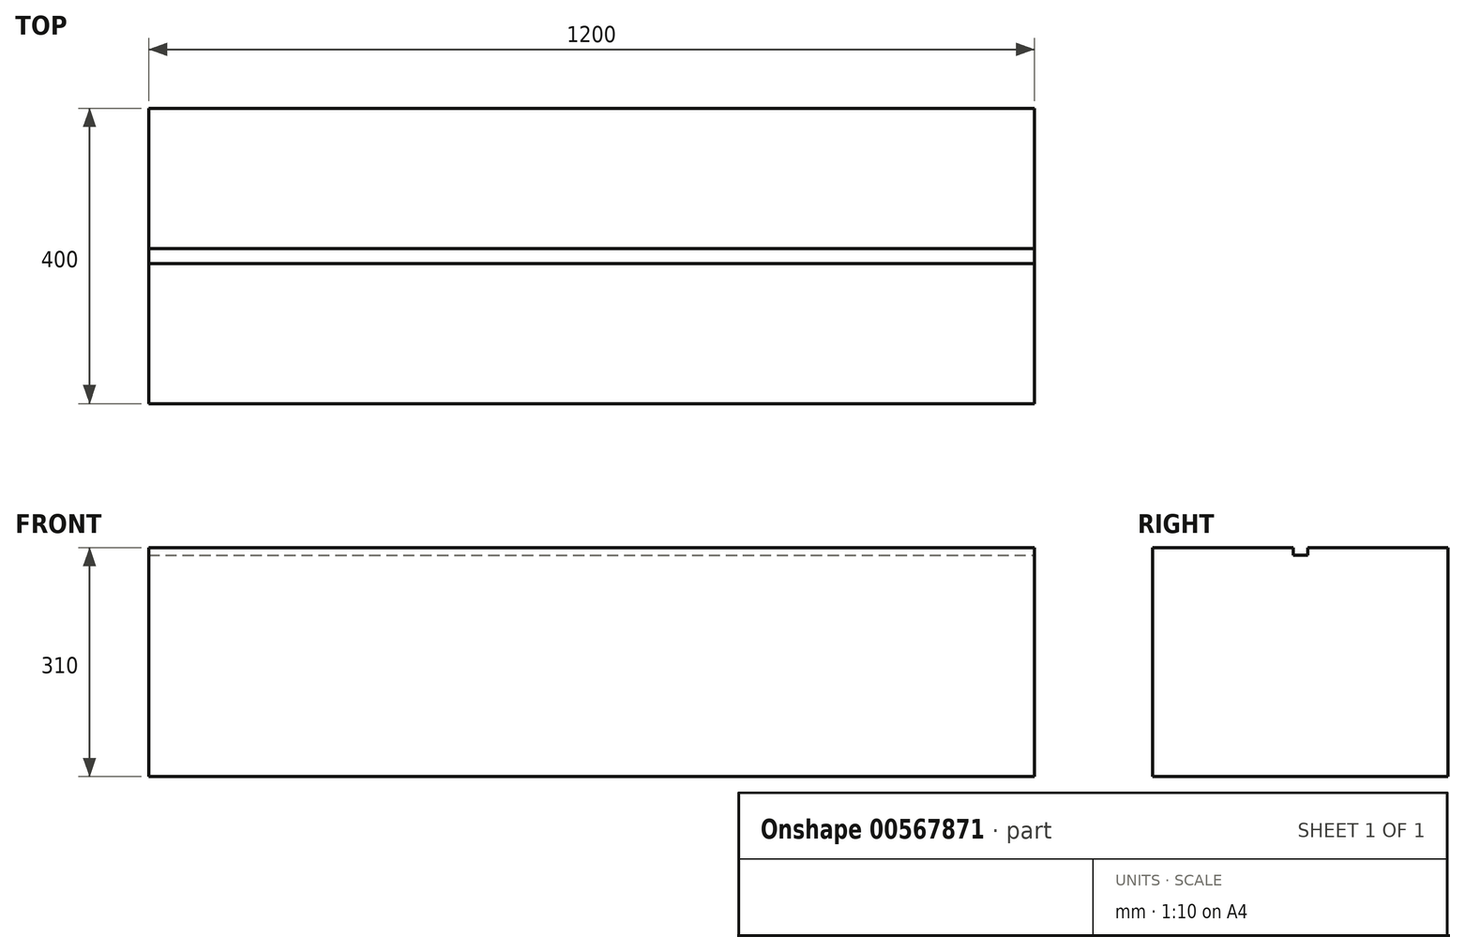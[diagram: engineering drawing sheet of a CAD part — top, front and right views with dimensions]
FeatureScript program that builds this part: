
annotation { "Feature Type Name" : "Feature", "Feature Type Description" : "" }
export const myFeature = defineFeature(function(context is Context, id is Id, definition is map)
    precondition{}
    {
        {
            var Q0;
            Q0=qCreatedBy(makeId("Right.planeOp"),FACE);
            var sketch = newSketch(context, id + "F0", { "sketchPlane" : qUnion([Q0])});
            skLineSegment(sketch, "E0.bottom", {"start": v(-160.6, 173.56) * mm, "end": v(239.4, 173.56) * mm});
            skLineSegment(sketch, "E0.top", {"start": v(-160.6, -136.44) * mm, "end": v(239.4, -136.44) * mm});
            skLineSegment(sketch, "E0.left", {"start": v(-160.6, 173.56) * mm, "end": v(-160.6, -136.44) * mm});
            skLineSegment(sketch, "E0.right", {"start": v(239.4, 173.56) * mm, "end": v(239.4, -136.44) * mm});
            skSolve(sketch);
        }
        {
            var Q0;
            Q0=qSketchRegion(id+"F0",true);
            extrude(context, id + "F1", {"entities" : qUnion([Q0]), "oppositeDirection" : true, "depth" : 1200 * mm, "offsetDistance" : 25 * mm});
        }
        {
            var Q0;
            Q0=makeQuery(id+"F1.opExtrude","CAP_FACE",FACE,{"disambiguationData":[OSD([sQuery(id+"F0.wireOp",EDGE,"E0.bottom"),sQuery(id+"F0.wireOp",EDGE,"E0.top"),sQuery(id+"F0.wireOp",EDGE,"E0.left"),sQuery(id+"F0.wireOp",EDGE,"E0.right")])],"isStart":true});
            var sketch = newSketch(context, id + "F2", { "sketchPlane" : qUnion([Q0])});
            skLineSegment(sketch, "E1.bottom", {"start": v(29.4, 173.56) * mm, "end": v(49.4, 173.56) * mm});
            skLineSegment(sketch, "E1.top", {"start": v(29.4, 163.56) * mm, "end": v(49.4, 163.56) * mm});
            skLineSegment(sketch, "E1.left", {"start": v(29.4, 173.56) * mm, "end": v(29.4, 163.56) * mm});
            skLineSegment(sketch, "E1.right", {"start": v(49.4, 173.56) * mm, "end": v(49.4, 163.56) * mm});
            skSolve(sketch);
        }
        {
            var Q0;
            Q0=makeQuery(id+"F2.imprint","IMPRINT",FACE,{"disambiguationData":[TD([[makeQuery(id+"F2.imprint","IMPRINT",EDGE,{"derivedFrom":sQuery(id+"F2.wireOp",EDGE,"E1.bottom")}),-1.0]])]});
            extrude(context, id + "F3", {"entities" : qUnion([Q0]), "operationType" : NewBodyOperationType.REMOVE, "oppositeDirection" : true, "depth" : 1250 * mm, "offsetDistance" : 25 * mm});
        }
    });
